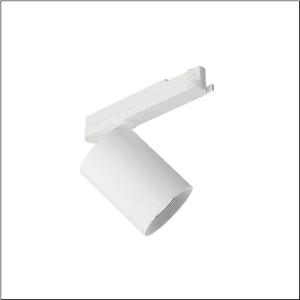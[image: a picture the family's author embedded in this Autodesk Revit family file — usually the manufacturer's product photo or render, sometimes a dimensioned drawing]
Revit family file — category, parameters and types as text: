
# Revit family: spot_21_51se12mbd5b
name_source: partatom
category: Lighting Fixtures
units: mm (PartAtom-declared; Revit-internal decimal feet)

## family parameters
Cut with Voids When Loaded = No
Host = Face
Light Source = No
Part Type = Normal
Room Calculation Point = No
Round Connector Dimension = Use Diameter
Shared = No

## types (1)
- --- (1 x LED, 5460 lm, 41.5 W, 4000K)
    Apparent Load = 42 VA
    CIE Flux Codes = 95 98 99 100 100
    Color Rendering = 90
    Color Temperature = 4000K
    Default Elevation = 1800 mm
    Description = Spot 21, directional spotlight, light control with lens, of PMMA, LED rated luminous flux: 5.250lm, light colour: 940, control gear: ECG Multilumen, with 3-phase adapter, mains connection: 220..240V, AC, 50/60Hz, of aluminium, traffic white (RAL 9016), length: 213mm, diameter: 105mm, protection rating (complete): IP20, insulation class (complete): insulation class I (protective earthing), certification: CE, impact resistance: IK02, permissible ambient temperature for indoor applications: -20..+40°C, packaging unit: 1 piece
    Height = 175 mm
    Lamp = 1 x LED
    Lamp Light Flux = 5460 lm
    Lamp Power = 41.5 W
    Lamp count = 1
    Length = 105 mm
    Luminous efficacy = 132 lm/W
    Manufacturer = Siteco
    ModVariant = No
    Model = 51SE12MBD5B
    Mounting Place = Ceiling
    Mounting Type = Pendant
    Number of Poles = 1
    OnlyDefault = Yes
    Power Factor = 1
    Product Name = Spot 21
    Product group = directional spotlight
    ProductGroupID = 905
    Protection Class = Protection class I
    Protection Degree = IP 20
    RLX_Detail_Level = 1
    RLX_Emergency_Light_Flux = 0 lm
    RLX_Emergency_Type = 0
    RLX_Emergency_Type_DB = No
    RlxData = <blob elided: 17629 chars, md5=e1776dc8>
    Socket = socket
    Standby Power = 0 W
    System Light Flux = 5460 lm
    System Power = 42 W
    Type Comments = factory setting: luminous flux: 100 % | (ON | ON | ON | ON) | 1050 mA
    Type Image = l_1003976.jpg
    URL = http://relux.com
    VarID = @adj_093969
    Voltage = 0 V
    Weight = 0.00 kg
    Width = 0 mm  [stored 0 ft]

note: [stored X ft] marks values corroborated as IEEE doubles in the binary element streams (Revit-internal decimal feet)

## geometry (parser evidence)
native form markers: Blend x4, Sweep x10
no freeform markers — native parametric forms only
